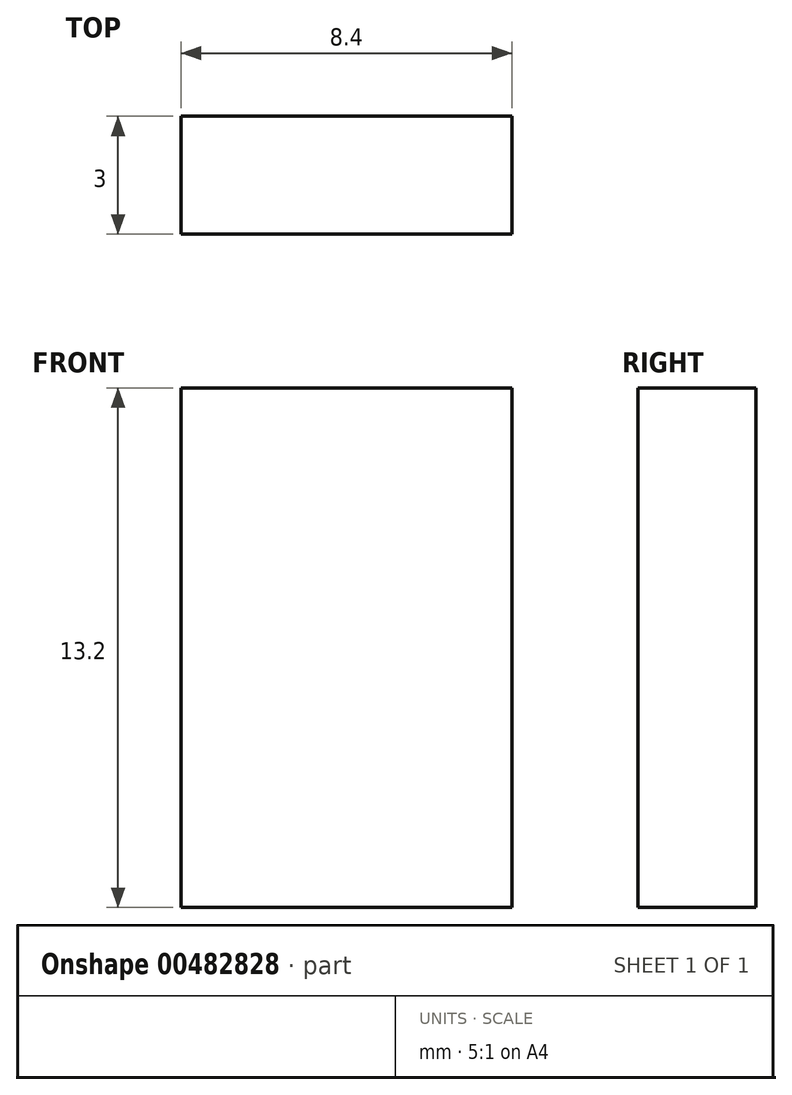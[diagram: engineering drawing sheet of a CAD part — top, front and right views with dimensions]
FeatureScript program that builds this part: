
annotation { "Feature Type Name" : "Feature", "Feature Type Description" : "" }
export const myFeature = defineFeature(function(context is Context, id is Id, definition is map)
    precondition{}
    {
        {
            var Q0;
            Q0=qCreatedBy(makeId("Top.planeOp"),FACE);
            var sketch = newSketch(context, id + "F0", { "sketchPlane" : qUnion([Q0])});
            skLineSegment(sketch, "E0.bottom", {"start": v(4.2, 1.5) * mm, "end": v(-4.2, 1.5) * mm});
            skLineSegment(sketch, "E0.top", {"start": v(4.2, -1.5) * mm, "end": v(-4.2, -1.5) * mm});
            skLineSegment(sketch, "E0.left", {"start": v(4.2, 1.5) * mm, "end": v(4.2, -1.5) * mm});
            skLineSegment(sketch, "E0.right", {"start": v(-4.2, 1.5) * mm, "end": v(-4.2, -1.5) * mm});
            skPoint(sketch, "E0.middle", {"position": v(0, 0) * mm});
            skSolve(sketch);
        }
        {
            var Q0;
            Q0=makeQuery(id+"F0.imprint","IMPRINT",FACE,{"disambiguationData":[TD([[makeQuery(id+"F0.imprint","IMPRINT",EDGE,{"derivedFrom":sQuery(id+"F0.wireOp",EDGE,"E0.bottom")}),1.0]])]});
            extrude(context, id + "F1", {"entities" : qUnion([Q0]), "depth" : 13.2 * mm});
        }
    });
